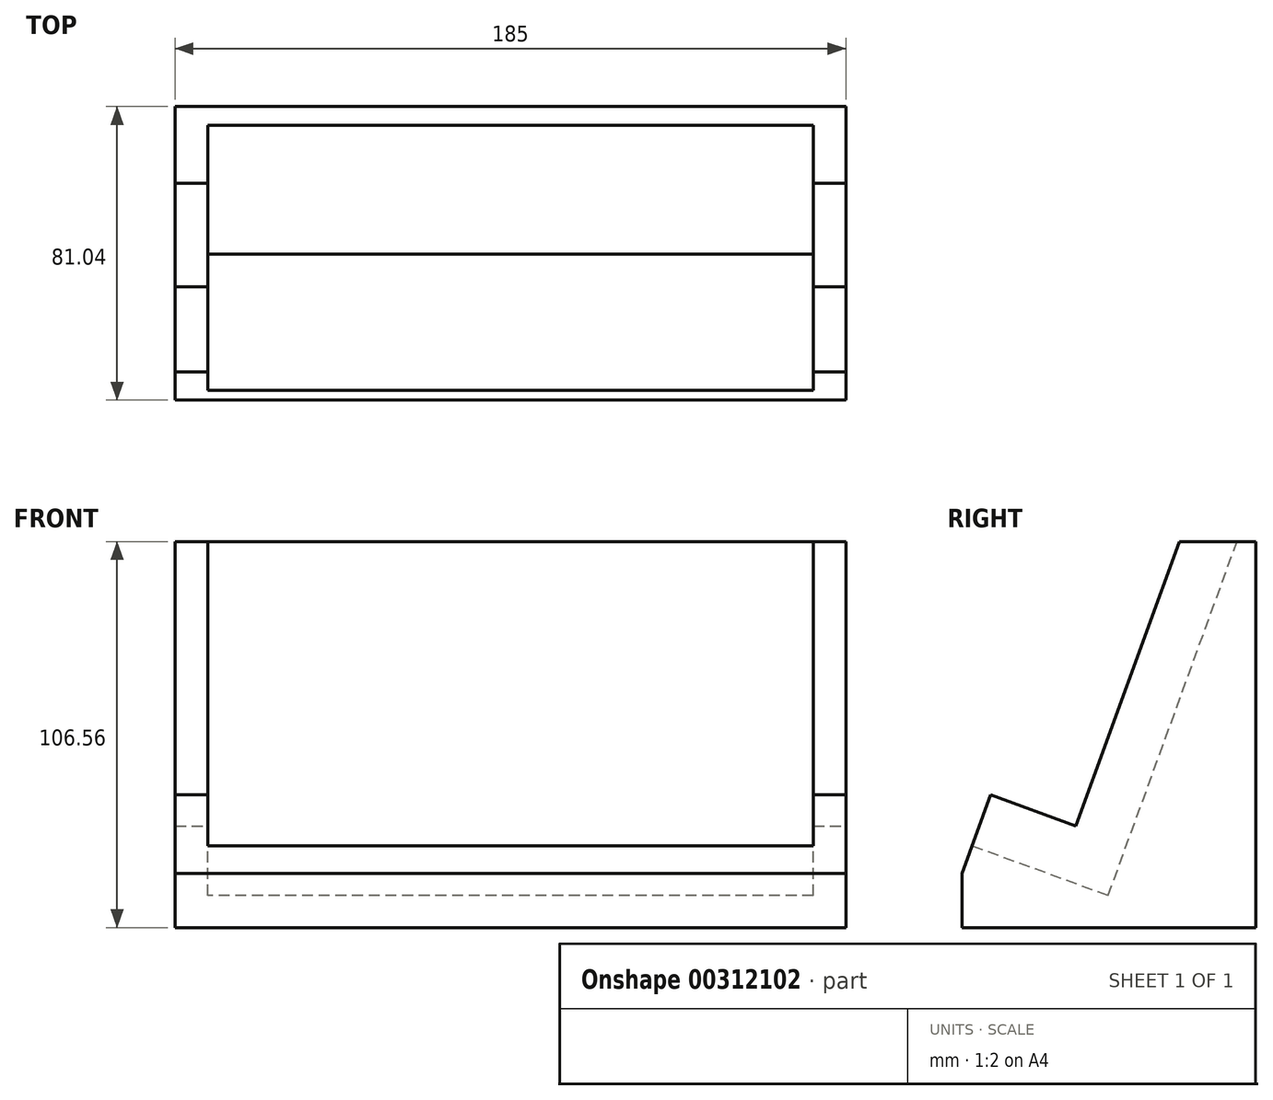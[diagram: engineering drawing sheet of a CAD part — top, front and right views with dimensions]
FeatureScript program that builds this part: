
annotation { "Feature Type Name" : "Feature", "Feature Type Description" : "" }
export const myFeature = defineFeature(function(context is Context, id is Id, definition is map)
    precondition{}
    {
        {
            var Q0;
            Q0=qCreatedBy(makeId("Right.planeOp"),FACE);
            var sketch = newSketch(context, id + "F0", { "sketchPlane" : qUnion([Q0])});
            skLineSegment(sketch, "E0", {"start": v(0, 0) * mm, "end": v(41.04, 0) * mm});
            skLineSegment(sketch, "E1", {"start": v(0, 0) * mm, "end": v(0, 77.2) * mm, "construction": true});
            skLineSegment(sketch, "E2", {"start": v(41.04, 0) * mm, "end": v(41.04, 112.76) * mm});
            skLineSegment(sketch, "E3", {"start": v(0, 0) * mm, "end": v(41.04, 112.76) * mm});
            skLineSegment(sketch, "E4.bottom", {"start": v(41.04, 0) * mm, "end": v(81.04, 0) * mm});
            skLineSegment(sketch, "E4.top", {"start": v(41.04, 112.76) * mm, "end": v(81.04, 112.76) * mm});
            skLineSegment(sketch, "E4.right", {"start": v(81.04, 0) * mm, "end": v(81.04, 112.76) * mm});
            skLineSegment(sketch, "E5.bottom", {"start": v(0, 0) * mm, "end": v(81.04, 0) * mm});
            skLineSegment(sketch, "E5.top", {"start": v(0, -15) * mm, "end": v(81.04, -15) * mm});
            skLineSegment(sketch, "E5.left", {"start": v(0, 0) * mm, "end": v(0, -15) * mm});
            skLineSegment(sketch, "E5.right", {"start": v(81.04, 0) * mm, "end": v(81.04, -15) * mm});
            skSolve(sketch);
        }
        {
            var Q0;
            Q0 = qSketchRegion(id + "F0", true);
            extrude(context, id + "F1", {"entities" : qUnion([Q0]), "endBound" : BoundingType.SYMMETRIC, "depth" : (55 * 3 + 20) * mm});
        }
        {
            var Q0;
            Q0=makeQuery(id+"F1.opExtrude","SWEPT_FACE",FACE,{"disambiguationData":[OSD([sQuery(id+"F0.wireOp",EDGE,"E3")])]});
            var sketch = newSketch(context, id + "F2", { "sketchPlane" : qUnion([Q0])});
            skLineSegment(sketch, "E6.0.0", {"start": v(-92.5, 120) * mm, "end": v(-92.5, 0) * mm, "construction": true});
            skLineSegment(sketch, "E6.0.1", {"start": v(-92.5, 0) * mm, "end": v(92.5, 0) * mm, "construction": true});
            skLineSegment(sketch, "E6.0.2", {"start": v(92.5, 0) * mm, "end": v(92.5, 120) * mm, "construction": true});
            skLineSegment(sketch, "E6.0.3", {"start": v(92.5, 120) * mm, "end": v(-92.5, 120) * mm, "construction": true});
            skLineSegment(sketch, "E7", {"start": v(-92.5, 120) * mm, "end": v(92.5, 0) * mm, "construction": true});
            skLineSegment(sketch, "E8", {"start": v(92.5, 120) * mm, "end": v(-92.5, 0) * mm, "construction": true});
            skPoint(sketch, "E9", {"position": v(0, 60) * mm});
            skLineSegment(sketch, "E10.bottom", {"start": v(83.5, 8) * mm, "end": v(-83.5, 8) * mm});
            skLineSegment(sketch, "E10.top", {"start": v(83.5, 112) * mm, "end": v(-83.5, 112) * mm});
            skLineSegment(sketch, "E10.left", {"start": v(83.5, 8) * mm, "end": v(83.5, 112) * mm});
            skLineSegment(sketch, "E10.right", {"start": v(-83.5, 8) * mm, "end": v(-83.5, 112) * mm});
            skSolve(sketch);
        }
        {
            var Q0;
            Q0=makeQuery(id+"F2.imprint","IMPRINT",FACE,{"disambiguationData":[TD([[makeQuery(id+"F2.imprint","IMPRINT",EDGE,{"derivedFrom":sQuery(id+"F2.wireOp",EDGE,"E10.bottom")}),-1.0]])]});
            extrude(context, id + "F3", {"entities" : qUnion([Q0]), "operationType" : NewBodyOperationType.REMOVE, "oppositeDirection" : true, "depth" : 40 * mm});
        }
        {
            var Q0;
            Q0=makeQuery(id+"F1.opExtrude","CAP_FACE",FACE,{"disambiguationData":[OSD([sQuery(id+"F0.wireOp",EDGE,"E3"),sQuery(id+"F0.wireOp",EDGE,"E4.top"),sQuery(id+"F0.wireOp",EDGE,"E4.right"),sQuery(id+"F0.wireOp",EDGE,"E5.top"),sQuery(id+"F0.wireOp",EDGE,"E5.left"),sQuery(id+"F0.wireOp",EDGE,"E5.right")])],"isStart":false});
            var sketch = newSketch(context, id + "F4", { "sketchPlane" : qUnion([Q0])});
            skLineSegment(sketch, "E11.0", {"start": v(75.9, 91.56) * mm, "end": v(38.3, 105.25) * mm, "construction": true});
            skLineSegment(sketch, "E12.0", {"start": v(40.32, -6.16) * mm, "end": v(75.9, 91.56) * mm, "construction": true});
            skLineSegment(sketch, "E13.0", {"start": v(41.04, 112.76) * mm, "end": v(81.04, 112.76) * mm, "construction": true});
            skLineSegment(sketch, "E14.bottom", {"start": v(100.15, 112.76) * mm, "end": v(33, 112.76) * mm});
            skLineSegment(sketch, "E14.top", {"start": v(100.15, 91.56) * mm, "end": v(33, 91.56) * mm});
            skLineSegment(sketch, "E14.left", {"start": v(100.15, 112.76) * mm, "end": v(100.15, 91.56) * mm});
            skLineSegment(sketch, "E14.right", {"start": v(33, 112.76) * mm, "end": v(33, 91.56) * mm});
            skSolve(sketch);
        }
        {
            var Q0;
            {var subQ3=sQuery(id+"F4.wireOp",EDGE,"E14.left");Q0=makeQuery(id+"F4.imprint","IMPRINT",FACE,{"disambiguationData":[TD([[makeQuery(id+"F4.imprint","IMPRINT",EDGE,{"derivedFrom":subQ3}),-1.0]])]});}
            var Q1;
            {var subQ0=sQuery(id+"F4.wireOp",EDGE,"E14.bottom");var subQ1=makeQuery(id+"F1.opExtrude","CAP_EDGE",EDGE,{"disambiguationData":[OSD([sQuery(id+"F0.wireOp",EDGE,"E3")])],"isStart":false});var subQ2=makeQuery(id+"F4.imprint","INTERSECT",VERTEX,{"derivedFrom":[subQ1,subQ0]});Q1=makeQuery(id+"F4.imprint","IMPRINT",FACE,{"disambiguationData":[TD([[makeQuery(id+"F4.imprint","IMPRINT",EDGE,{"disambiguationData":[TD([[subQ2,1.0]])],"derivedFrom":subQ1}),-1.0]])]});}
            var Q2;
            {var subQ3=sQuery(id+"F4.wireOp",EDGE,"E14.right");Q2=makeQuery(id+"F4.imprint","IMPRINT",FACE,{"disambiguationData":[TD([[makeQuery(id+"F4.imprint","IMPRINT",EDGE,{"derivedFrom":subQ3}),1.0]])]});}
            extrude(context, id + "F5", {"entities" : qUnion([Q0, Q1, Q2]), "operationType" : NewBodyOperationType.REMOVE, "oppositeDirection" : true, "depth" : 200 * mm});
        }
        {
            var Q0;
            Q0=makeQuery(id+"F1.opExtrude","CAP_FACE",FACE,{"disambiguationData":[OSD([sQuery(id+"F0.wireOp",EDGE,"E3"),sQuery(id+"F0.wireOp",EDGE,"E4.top"),sQuery(id+"F0.wireOp",EDGE,"E4.right"),sQuery(id+"F0.wireOp",EDGE,"E5.top"),sQuery(id+"F0.wireOp",EDGE,"E5.left"),sQuery(id+"F0.wireOp",EDGE,"E5.right")])],"isStart":false});
            var sketch = newSketch(context, id + "F6", { "sketchPlane" : qUnion([Q0])});
            skLineSegment(sketch, "E15.0", {"start": v(0, 0) * mm, "end": v(33.33, 91.56) * mm, "construction": true});
            skLineSegment(sketch, "E16.0", {"start": v(81.04, 91.56) * mm, "end": v(33.33, 91.56) * mm, "construction": true});
            skLineSegment(sketch, "E17.0", {"start": v(40.32, -6.16) * mm, "end": v(75.9, 91.56) * mm, "construction": true});
            skLineSegment(sketch, "E18.0", {"start": v(40.32, -6.16) * mm, "end": v(2.74, 7.52) * mm, "construction": true});
            skLineSegment(sketch, "E19", {"start": v(7.87, 21.61) * mm, "end": v(45.45, 7.93) * mm});
            skLineSegment(sketch, "E20", {"start": v(59.93, 91.56) * mm, "end": v(26.23, -1.03) * mm});
            skLineSegment(sketch, "E21", {"start": v(33.33, 91.56) * mm, "end": v(59.93, 91.56) * mm});
            skLineSegment(sketch, "E22", {"start": v(33.33, 91.56) * mm, "end": v(7.87, 21.61) * mm});
            skSolve(sketch);
        }
        {
            var Q0;
            {var subQ4=sQuery(id+"F6.wireOp",EDGE,"E21");Q0=makeQuery(id+"F6.imprint","IMPRINT",FACE,{"disambiguationData":[TD([[makeQuery(id+"F6.imprint","IMPRINT",EDGE,{"derivedFrom":subQ4}),1.0]])]});}
            extrude(context, id + "F7", {"entities" : qUnion([Q0]), "operationType" : NewBodyOperationType.REMOVE, "oppositeDirection" : true, "depth" : 200 * mm});
        }
    });
